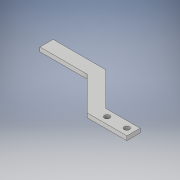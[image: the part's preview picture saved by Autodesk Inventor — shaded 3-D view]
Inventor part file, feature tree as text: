
AUTODESK INVENTOR PART (.ipt)
format: ipt  version: 2019 (Build 230136000, 136)  size: 115,200 bytes
history: native  units: mm
features: extrude x1, sketch x1
ambient origin geometry x8: Origin, YZ Plane, XZ Plane, XY Plane, X Axis, Y Axis, Z Axis, Center Point
bodies: Body1 (feature_tree)
feature tree (2):
  extrude  "Extrusion4"  Depth=40.0mm
  sketch  "Sketch1"  dims[d0=10.0mm d1=40.0mm d2=135.0deg d3=40.0mm d4=10.0mm d14=45.0deg d15=10.0mm d16=30.0mm d17=4.0mm d18=10.0mm d19=5.0mm d22=4.0mm d23=5.0mm d24=5.0mm d25=3.18mm d26=0.0mm]
